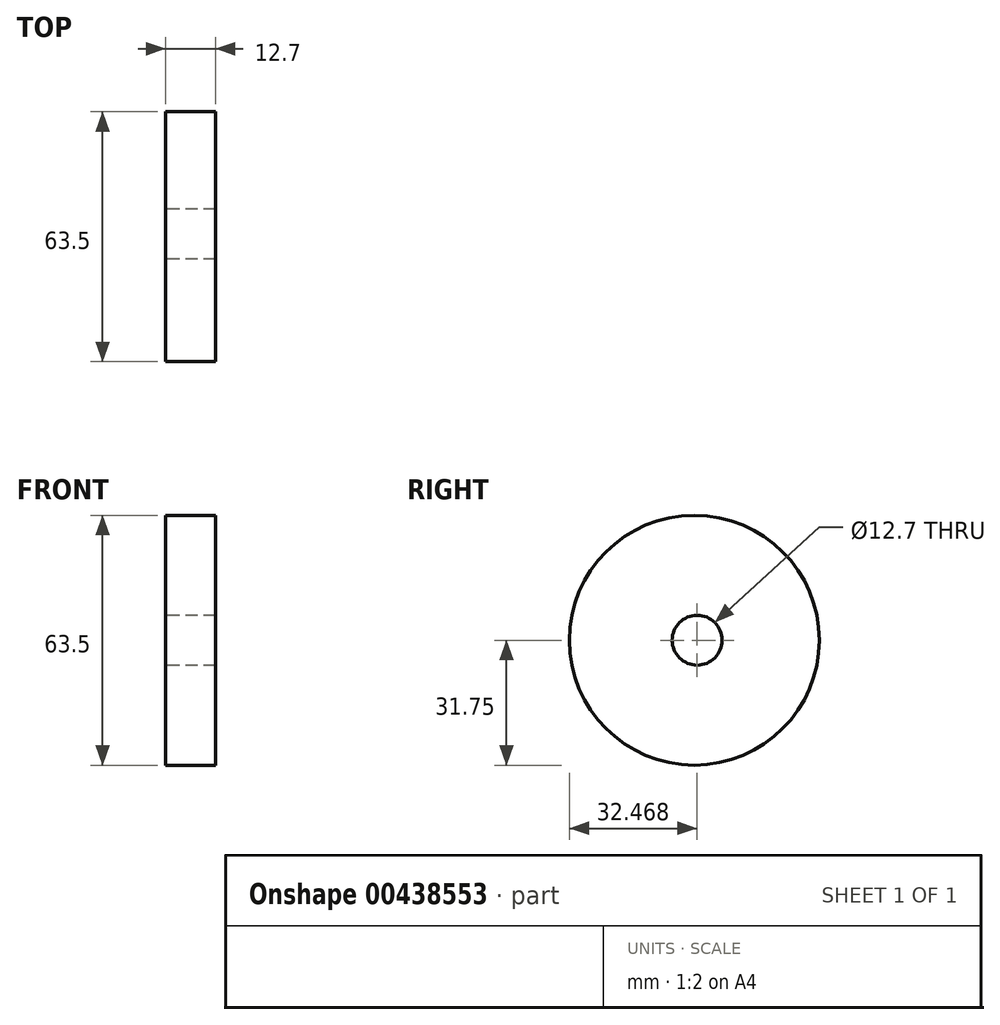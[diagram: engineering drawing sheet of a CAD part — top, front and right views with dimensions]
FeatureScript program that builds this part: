
annotation { "Feature Type Name" : "Feature", "Feature Type Description" : "" }
export const myFeature = defineFeature(function(context is Context, id is Id, definition is map)
    precondition{}
    {
        {
            var Q0;
            Q0=qCreatedBy(makeId("Right.planeOp"),FACE);
            var sketch = newSketch(context, id + "F0", { "sketchPlane" : qUnion([Q0])});
            skCircle(sketch, "E0", {"center": v(0, 0) * mm, "radius": 31.75 * mm});
            skCircle(sketch, "E1", {"center": v(0.72, 0) * mm, "radius": 6.35 * mm});
            skSolve(sketch);
        }
        {
            var Q0;
            Q0=makeQuery(id+"F0.imprint","IMPRINT",FACE,{"disambiguationData":[TD([[makeQuery(id+"F0.imprint","IMPRINT",EDGE,{"derivedFrom":sQuery(id+"F0.wireOp",EDGE,"E0")}),1.0]])]});
            extrude(context, id + "F1", {"entities" : qUnion([Q0]), "depth" : 12.7 * mm});
        }
    });
